# Revit family: Tina Bañaseo
name_source: partatom
category: Plumbing Fixtures
revit_build: Autodesk Revit 2015 (Build: 20140322_1515(x64)
units: mm (PartAtom-declared; Revit-internal decimal feet)

## types (1)
- Tina Bañaseo
    Assembly Code = D2010.60
    BIMobject category = Bath & Spas
    BT_Color = Blanco
    BT_Itemizado_Estandar_CDT = E 04 02 03
    BT_Material = Acero
    BT_SKU = 00 00 00
    BT_Uso = Baño
    Depth = 700 mm
    Description = BAÑASEO DE ACERO
    Drain Diameter = 52 mm
    Edition number = 0
    Height = 422 mm
    ID_Objeto = BT_F_F_1780
    ID_Source = BIMTOOL
    IFC Classification = Furnishing Element
    Imported Category Visibility 01 = Yes
    Imported Category Visibility 02 = No
    Inside height (mm) = 372 mm
    Inside length (mm) = 875 mm
    Inside width (mm) = 575 mm
    Installation structure = Naked
    Installation type = Drop-in
    Keynote = 22 41 19
    Manufacturer = Roca
    Manufacturer name = Roca
    Material = Steel
    Model = Tina Bañaseo
    NBS Reference Code = 35-06-08
    NBS Reference Description = Baths
    Nominal height = 390.00
    Nominal width = 700.00
    Overflow Diameter = 52 mm
    People capacity = 1
    Primary Material = Acero
    Product SKU = A213100001
    Product family = Ba??????aseo|Contesa
    Product group = BATHS
    Shape = Rectangular
    Sound insulation = Yes
    Supplier = Mk
    Tapholes Diameters = 0 mm
    Type Comments = BAÑASEO DE ACERO
    UNSPSC Code = 30181501
    URL = http://www.roca.com
    Uniclass 1.4 Code = L7211
    Uniclass 1.4 Description = Baths
    Uniclass 2.0 Code = PR-35-06-08
    Uniclass 2.0 Description = Baths
    Water capacity (L) = 90
    Weight Net (Kg) = 0
    Width = 1000 mm

## geometry (parser evidence)
native form markers: Blend x6, Extrusion x3, Sweep x15
no freeform markers — native parametric forms only
